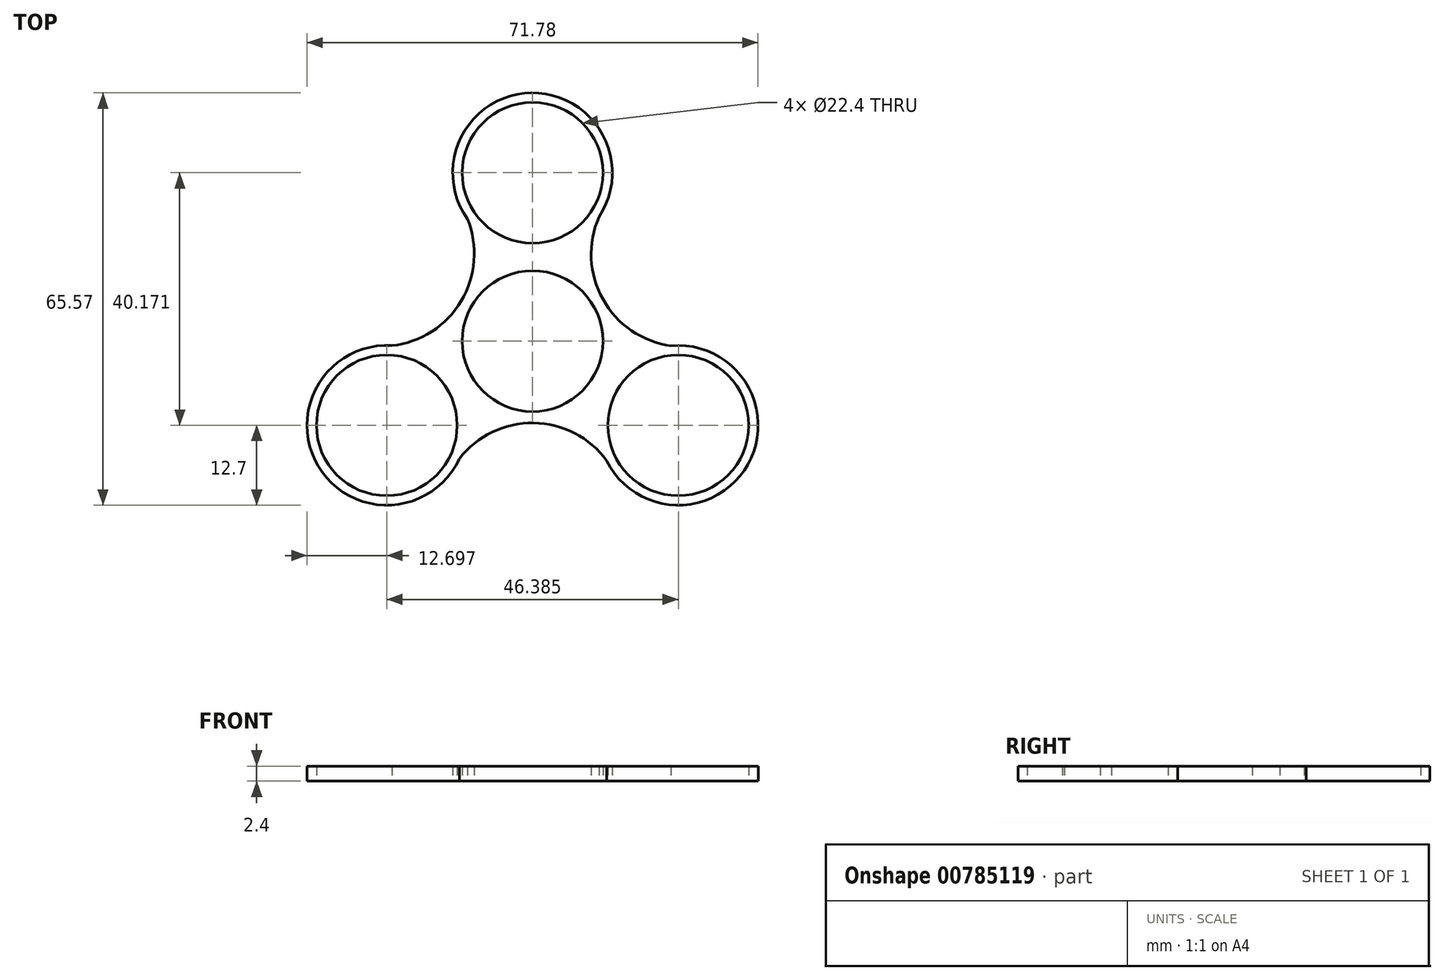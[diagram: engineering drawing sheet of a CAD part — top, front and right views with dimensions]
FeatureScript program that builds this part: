
annotation { "Feature Type Name" : "Feature", "Feature Type Description" : "" }
export const myFeature = defineFeature(function(context is Context, id is Id, definition is map)
    precondition{}
    {
        {
            var Q0;
            Q0=qCreatedBy(makeId("Top.planeOp"),FACE);
            var sketch = newSketch(context, id + "F0", { "sketchPlane" : qUnion([Q0])});
            skCircle(sketch, "E0", {"center": v(0, 0) * mm, "radius": 11.2 * mm});
            skCircle(sketch, "E1", {"center": v(0, 26.78) * mm, "radius": 11.2 * mm});
            skArc(sketch, "E2", {"start": v(10.58, 19.75) * mm, "mid": v(-0.18, 39.48) * mm, "end": v(-10.38, 19.46) * mm});
            skCircle(sketch, "E3.1.0", {"center": v(-23.2, -13.4) * mm, "radius": 11.2 * mm});
            skArc(sketch, "E3.1.1", {"start": v(-22.4, -0.72) * mm, "mid": v(-34.1, -19.9) * mm, "end": v(-11.66, -18.72) * mm});
            skCircle(sketch, "E3.2.0", {"center": v(23.2, -13.4) * mm, "radius": 11.2 * mm});
            skArc(sketch, "E3.2.1", {"start": v(11.82, -19.04) * mm, "mid": v(34.28, -19.59) * mm, "end": v(22.04, -0.74) * mm});
            skArc(sketch, "E4", {"start": v(10.58, 19.75) * mm, "mid": v(11.2, 6.65) * mm, "end": v(22.04, -0.74) * mm});
            skArc(sketch, "E5.1.0", {"start": v(-22.4, -0.72) * mm, "mid": v(-11.36, 6.38) * mm, "end": v(-10.38, 19.46) * mm});
            skArc(sketch, "E5.2.0", {"start": v(11.82, -19.04) * mm, "mid": v(0.16, -13.02) * mm, "end": v(-11.66, -18.72) * mm});
            skLineSegment(sketch, "E6.trimOffspring", {"start": v(11.04, 6.29) * mm, "end": v(11.63, 6.63) * mm});
            skSolve(sketch);
        }
        {
            var Q0;
            Q0=makeQuery(id+"F0.imprint","IMPRINT",FACE,{"disambiguationData":[TD([[makeQuery(id+"F0.imprint","IMPRINT",EDGE,{"derivedFrom":sQuery(id+"F0.wireOp",EDGE,"E0")}),-1.0]])]});
            extrude(context, id + "F1", {"entities" : qUnion([Q0]), "depth" : 2.4 * mm, "offsetDistance" : 25 * mm});
        }
    });
